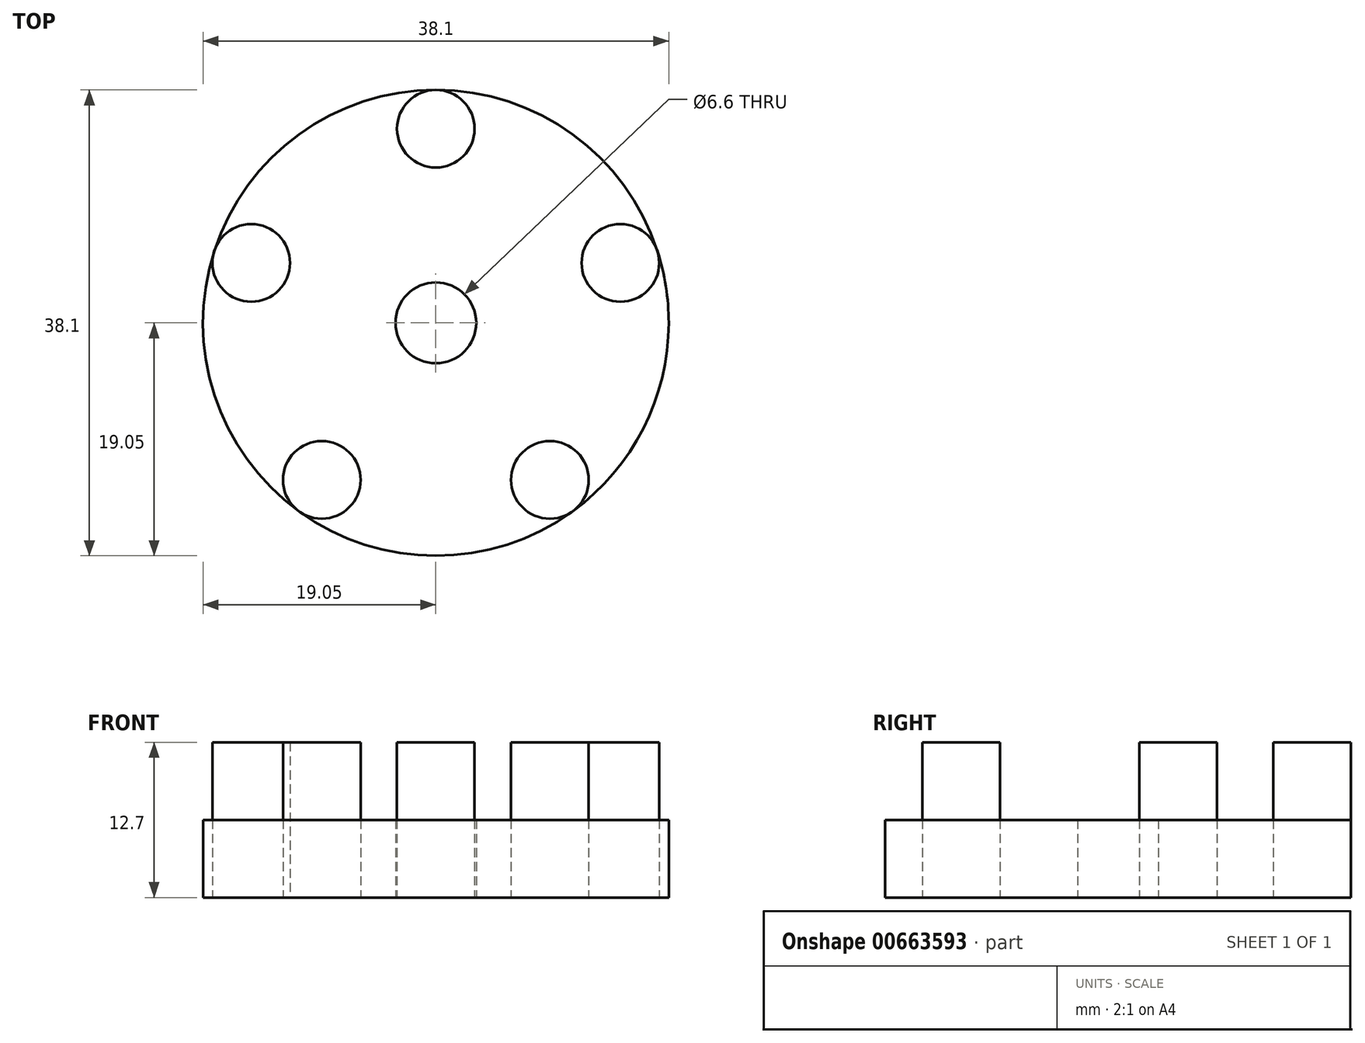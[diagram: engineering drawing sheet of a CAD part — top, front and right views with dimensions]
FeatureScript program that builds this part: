
annotation { "Feature Type Name" : "Feature", "Feature Type Description" : "" }
export const myFeature = defineFeature(function(context is Context, id is Id, definition is map)
    precondition{}
    {
        {
            var Q0;
            Q0=qCreatedBy(makeId("Top.planeOp"),FACE);
            var sketch = newSketch(context, id + "F0", { "sketchPlane" : qUnion([Q0])});
            skCircle(sketch, "E0", {"center": v(0, 0) * mm, "radius": 19.05 * mm});
            skLineSegment(sketch, "E1", {"start": v(0, 19.05) * mm, "end": v(0, 15.88) * mm, "construction": true});
            skCircle(sketch, "E2", {"center": v(0, 15.88) * mm, "radius": 3.18 * mm});
            skCircle(sketch, "E3.1.0", {"center": v(-15.1, 4.9) * mm, "radius": 3.18 * mm});
            skCircle(sketch, "E3.2.0", {"center": v(-9.33, -12.84) * mm, "radius": 3.18 * mm});
            skCircle(sketch, "E3.3.0", {"center": v(9.33, -12.84) * mm, "radius": 3.18 * mm});
            skCircle(sketch, "E3.4.0", {"center": v(15.1, 4.9) * mm, "radius": 3.18 * mm});
            skCircle(sketch, "E4", {"center": v(0, 0) * mm, "radius": 3.3 * mm});
            skSolve(sketch);
        }
        {
            var Q0;
            Q0 = qSketchRegion(id + "F0", true);
            extrude(context, id + "F1", {"entities" : qUnion([Q0]), "depth" : 6.35 * mm, "offsetDistance" : 25.4 * mm});
        }
        {
            var Q0;
            Q0=makeQuery(id+"F0.imprint","IMPRINT",FACE,{"disambiguationData":[TD([[makeQuery(id+"F0.imprint","IMPRINT",EDGE,{"derivedFrom":sQuery(id+"F0.wireOp",EDGE,"E2")}),1.0]])]});
            var Q1;
            Q1=makeQuery(id+"F0.imprint","IMPRINT",FACE,{"disambiguationData":[TD([[makeQuery(id+"F0.imprint","IMPRINT",EDGE,{"derivedFrom":sQuery(id+"F0.wireOp",EDGE,"E3.2.0")}),1.0]])]});
            var Q2;
            Q2=makeQuery(id+"F0.imprint","IMPRINT",FACE,{"disambiguationData":[TD([[makeQuery(id+"F0.imprint","IMPRINT",EDGE,{"derivedFrom":sQuery(id+"F0.wireOp",EDGE,"E3.3.0")}),1.0]])]});
            var Q3;
            Q3=makeQuery(id+"F0.imprint","IMPRINT",FACE,{"disambiguationData":[TD([[makeQuery(id+"F0.imprint","IMPRINT",EDGE,{"derivedFrom":sQuery(id+"F0.wireOp",EDGE,"E3.4.0")}),1.0]])]});
            var Q4;
            Q4=sQuery(id+"F0.wireOp",EDGE,"E2");
            var Q5;
            Q5=sQuery(id+"F0.wireOp",EDGE,"E3.1.0");
            var Q6;
            Q6=sQuery(id+"F0.wireOp",EDGE,"E3.2.0");
            var Q7;
            Q7=sQuery(id+"F0.wireOp",EDGE,"E3.3.0");
            var Q8;
            Q8=sQuery(id+"F0.wireOp",EDGE,"E3.4.0");
            extrude(context, id + "F2", {"entities" : qUnion([Q0, Q1, Q2, Q3]), "surfaceEntities" : qUnion([Q4, Q5, Q6, Q7, Q8]), "depth" : 12.7 * mm, "offsetDistance" : 25.4 * mm});
        }
        {
            var Q0;
            Q0=makeQuery(id+"F0.imprint","IMPRINT",FACE,{"disambiguationData":[TD([[makeQuery(id+"F0.imprint","IMPRINT",EDGE,{"derivedFrom":sQuery(id+"F0.wireOp",EDGE,"E3.1.0")}),1.0]])]});
            var Q1;
            Q1=sQuery(id+"F0.wireOp",EDGE,"E3.1.0");
            extrude(context, id + "F3", {"entities" : qUnion([Q0]), "surfaceEntities" : qUnion([Q1]), "depth" : 12.7 * mm, "offsetDistance" : 25.4 * mm});
        }
    });
